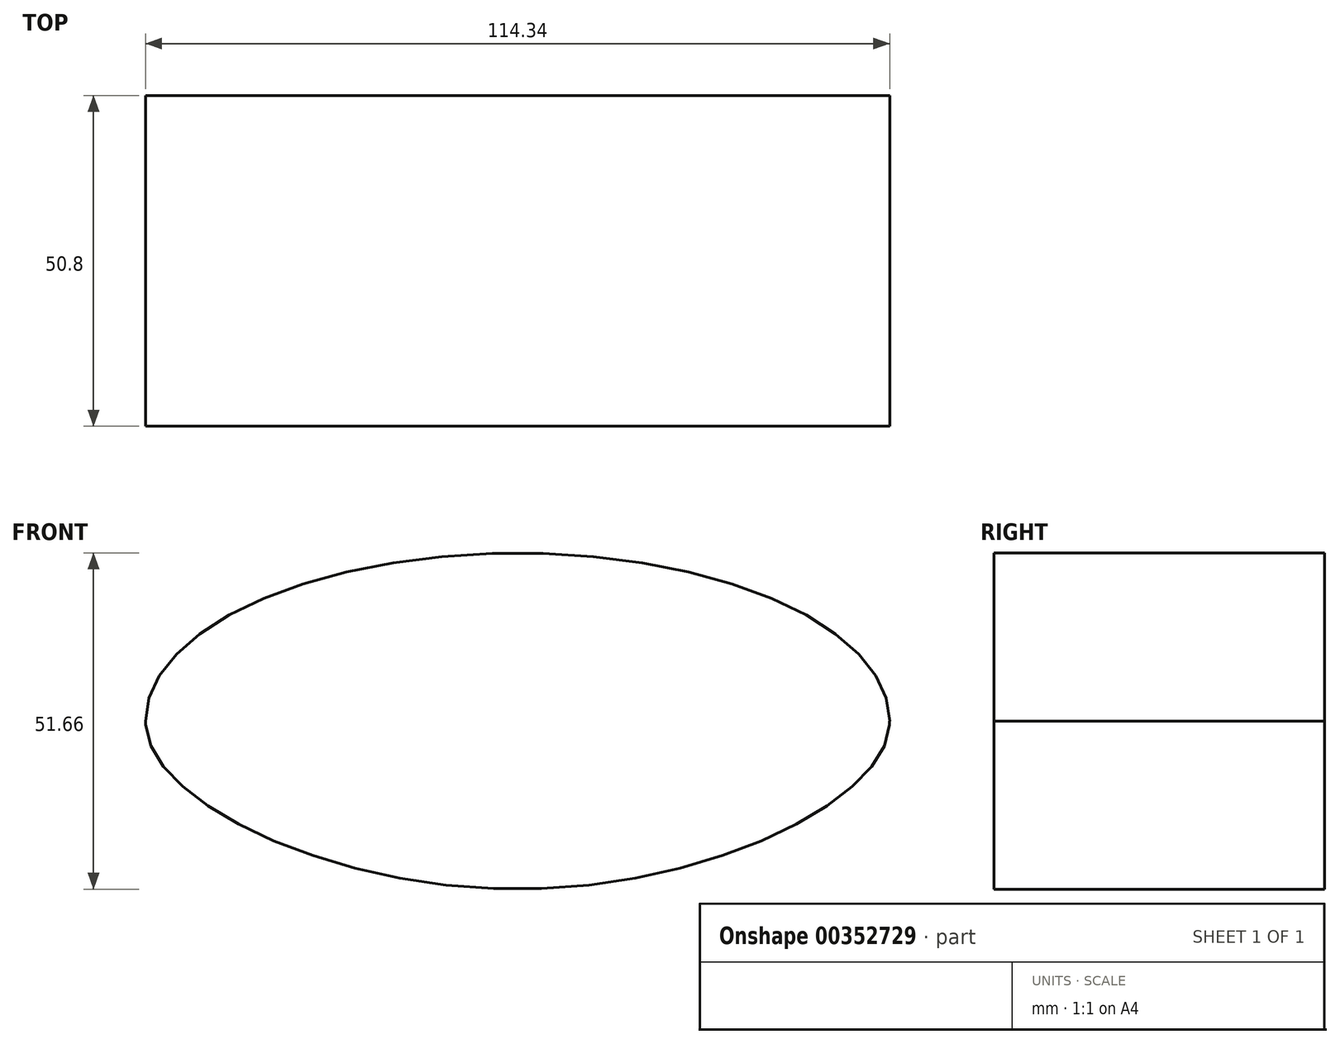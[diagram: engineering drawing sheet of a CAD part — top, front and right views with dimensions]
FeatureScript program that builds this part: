
annotation { "Feature Type Name" : "Feature", "Feature Type Description" : "" }
export const myFeature = defineFeature(function(context is Context, id is Id, definition is map)
    precondition{}
    {
        {
            var Q0;
            Q0=qCreatedBy(makeId("Front.planeOp"),FACE);
            var sketch = newSketch(context, id + "F0", { "sketchPlane" : qUnion([Q0])});
            skEllipticalArc(sketch, "E0", {});
            skFitSpline(sketch, "E1", {"points": [v(-57.17, 0) * mm, v(0, 23.45) * mm, v(57.17, 0) * mm, v(0, -25.83) * mm, v(-57.17, 0) * mm]});
            const initialGuessF0  = {"E0": [0, 0, 1, 0, 0.05716539346255082, 0.02582647460882771, 6.259977916941779, 3.1648000438276136]};
            skSetInitialGuess(sketch, initialGuessF0);
            skSolve(sketch);
        }
        {
            var Q0;
            Q0=qSketchRegion(id+"F0",true);
            extrude(context, id + "F1", {"entities" : qUnion([Q0]), "depth" : 50.8 * mm});
        }
    });
